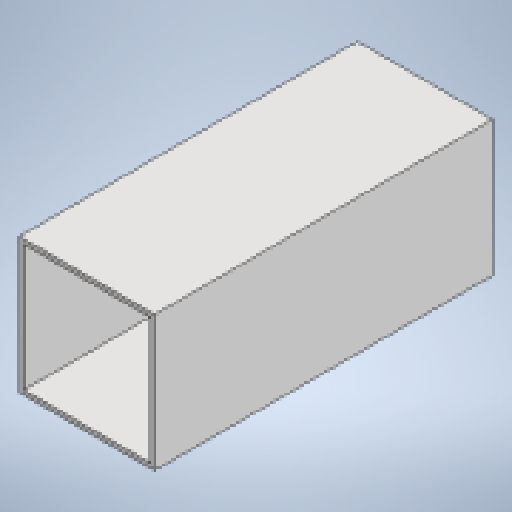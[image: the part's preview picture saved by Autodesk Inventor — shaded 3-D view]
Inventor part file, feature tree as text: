
AUTODESK INVENTOR PART (.ipt)
format: ipt  version: 2025.1 (Build 291241020, 241B)  size: 152,064 bytes
history: native  units: mm
features: extrude x1, sketch x1
ambient origin geometry x8: Origin, YZ Plane, XZ Plane, XY Plane, X Axis, Y Axis, Z Axis, Center Point
bodies: Body1 (feature_tree)
feature tree (2):
  extrude  "Extrusion3"  Depth=60.0mm
  sketch  "Sketch9"  dims[d61=500.0mm d172=60.0mm d173=60.0mm d174=2.0mm d175=150.0mm d176=0.0mm]
